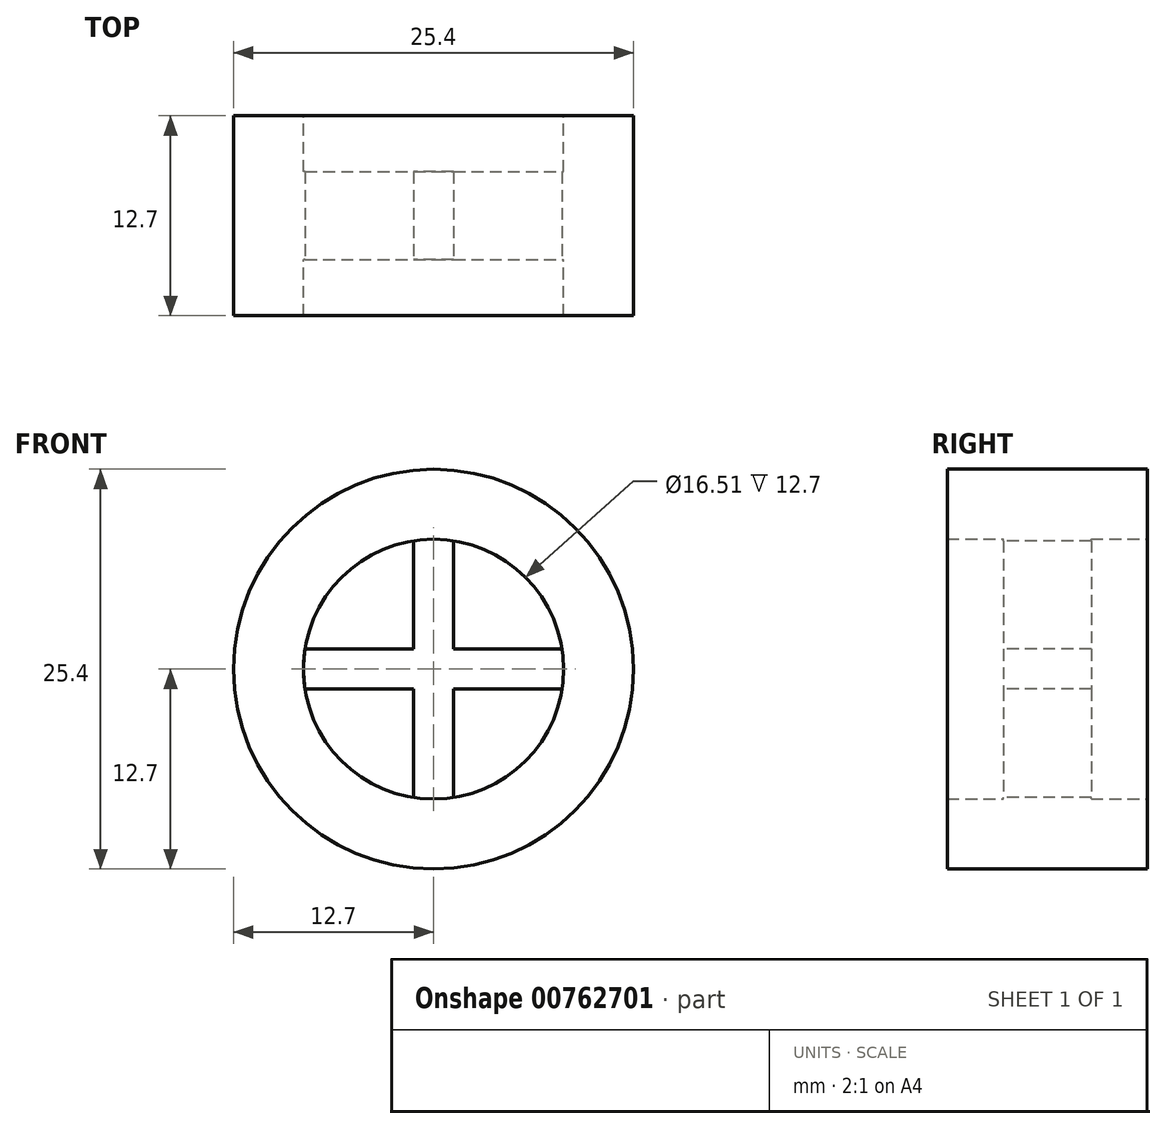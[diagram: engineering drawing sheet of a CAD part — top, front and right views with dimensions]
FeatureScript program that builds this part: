
annotation { "Feature Type Name" : "Feature", "Feature Type Description" : "" }
export const myFeature = defineFeature(function(context is Context, id is Id, definition is map)
    precondition{}
    {
        {
            var Q0;
            Q0=qCreatedBy(makeId("Front.planeOp"),FACE);
            var sketch = newSketch(context, id + "F0", { "sketchPlane" : qUnion([Q0])});
            skLineSegment(sketch, "E0", {"start": v(-26.37, 14.82) * mm, "end": v(-26.37, 24.82) * mm});
            skLineSegment(sketch, "E1", {"start": v(-26.37, 24.82) * mm, "end": v(-13.23, 24.82) * mm});
            skLineSegment(sketch, "E2", {"start": v(-13.23, 24.82) * mm, "end": v(-13.23, 15) * mm});
            skLineSegment(sketch, "E3", {"start": v(-13.23, 15) * mm, "end": v(-26.37, 14.82) * mm});
            skCircle(sketch, "E4", {"center": v(13.48, 17.4) * mm, "radius": 5.12 * mm});
            skPoint(sketch, "E4.first.point", {"position": v(10.66, 21.67) * mm});
            skPoint(sketch, "E4.second.point", {"position": v(16.03, 12.97) * mm});
            skPoint(sketch, "E4.third.point", {"position": v(17.5, 20.56) * mm});
            skLineSegment(sketch, "E5", {"start": v(10.66, 21.67) * mm, "end": v(13.48, 17.4) * mm});
            skLineSegment(sketch, "E6", {"start": v(17.5, 20.56) * mm, "end": v(13.48, 17.4) * mm});
            skLineSegment(sketch, "E7", {"start": v(13.48, 17.4) * mm, "end": v(16.03, 12.97) * mm});
            skLineSegment(sketch, "E8", {"start": v(9.35, 14.39) * mm, "end": v(13.48, 17.4) * mm});
            skCircle(sketch, "E9", {"center": v(0, 0) * mm, "radius": 12.7 * mm});
            skCircle(sketch, "E10", {"center": v(0, 0) * mm, "radius": 8.26 * mm});
            skLineSegment(sketch, "E11", {"start": v(-8.26, 0) * mm, "end": v(8.26, 0) * mm});
            skLineSegment(sketch, "E12", {"start": v(0, 8.26) * mm, "end": v(0, -8.26) * mm});
            skLineSegment(sketch, "E13", {"start": v(-1.27, 8.16) * mm, "end": v(-1.27, -8.26) * mm});
            skLineSegment(sketch, "E14", {"start": v(1.27, 8.16) * mm, "end": v(1.27, -8.16) * mm});
            skLineSegment(sketch, "E15", {"start": v(-8.16, 1.27) * mm, "end": v(8.16, 1.27) * mm});
            skLineSegment(sketch, "E16", {"start": v(-8.16, -1.27) * mm, "end": v(8.16, -1.27) * mm});
            skSolve(sketch);
        }
        {
            var Q0;
            Q0=makeQuery(id+"F0.imprint","IMPRINT",FACE,{"disambiguationData":[TD([[makeQuery(id+"F0.imprint","IMPRINT",EDGE,{"derivedFrom":sQuery(id+"F0.wireOp",EDGE,"E9")}),1.0]])]});
            extrude(context, id + "F1", {"entities" : qUnion([Q0]), "endBound" : BoundingType.SYMMETRIC, "depth" : 12.7 * mm, "offsetDistance" : 25.4 * mm});
        }
        {
            var Q0;
            {var subQ0=sQuery(id+"F0.wireOp",EDGE,"E12");var subQ1=sQuery(id+"F0.wireOp",EDGE,"E10");var subQ2=makeQuery(id+"F0.imprint","INTERSECT",VERTEX,{"disambiguationData":[OD(0.0)],"derivedFrom":[subQ1,subQ0]});Q0=makeQuery(id+"F0.imprint","IMPRINT",FACE,{"disambiguationData":[TD([[makeQuery(id+"F0.imprint","IMPRINT",EDGE,{"disambiguationData":[TD([[subQ2,1.0]])],"derivedFrom":subQ1}),1.0]])]});}
            var Q1;
            {var subQ0=sQuery(id+"F0.wireOp",EDGE,"E12");var subQ1=sQuery(id+"F0.wireOp",EDGE,"E10");var subQ2=makeQuery(id+"F0.imprint","INTERSECT",VERTEX,{"disambiguationData":[OD(0.0)],"derivedFrom":[subQ1,subQ0]});Q1=makeQuery(id+"F0.imprint","IMPRINT",FACE,{"disambiguationData":[TD([[makeQuery(id+"F0.imprint","IMPRINT",EDGE,{"disambiguationData":[TD([[subQ2,-1.0]])],"derivedFrom":subQ1}),1.0]])]});}
            var Q2;
            {var subQ0=sQuery(id+"F0.wireOp",EDGE,"E13");var subQ1=sQuery(id+"F0.wireOp",EDGE,"E11");var subQ2=makeQuery(id+"F0.imprint","INTERSECT",VERTEX,{"derivedFrom":[subQ1,subQ0]});Q2=makeQuery(id+"F0.imprint","IMPRINT",FACE,{"disambiguationData":[TD([[makeQuery(id+"F0.imprint","IMPRINT",EDGE,{"disambiguationData":[TD([[subQ2,-1.0]])],"derivedFrom":subQ1}),1.0]])]});}
            var Q3;
            {var subQ0=sQuery(id+"F0.wireOp",EDGE,"E12");var subQ1=sQuery(id+"F0.wireOp",EDGE,"E11");var subQ2=makeQuery(id+"F0.imprint","INTERSECT",VERTEX,{"derivedFrom":[subQ1,subQ0]});Q3=makeQuery(id+"F0.imprint","IMPRINT",FACE,{"disambiguationData":[TD([[makeQuery(id+"F0.imprint","IMPRINT",EDGE,{"disambiguationData":[TD([[subQ2,-1.0]])],"derivedFrom":subQ1}),1.0]])]});}
            var Q4;
            {var subQ0=sQuery(id+"F0.wireOp",EDGE,"E12");var subQ1=sQuery(id+"F0.wireOp",EDGE,"E11");var subQ2=makeQuery(id+"F0.imprint","INTERSECT",VERTEX,{"derivedFrom":[subQ1,subQ0]});Q4=makeQuery(id+"F0.imprint","IMPRINT",FACE,{"disambiguationData":[TD([[makeQuery(id+"F0.imprint","IMPRINT",EDGE,{"disambiguationData":[TD([[subQ2,-1.0]])],"derivedFrom":subQ1}),-1.0]])]});}
            var Q5;
            {var subQ0=sQuery(id+"F0.wireOp",EDGE,"E13");var subQ1=sQuery(id+"F0.wireOp",EDGE,"E11");var subQ2=makeQuery(id+"F0.imprint","INTERSECT",VERTEX,{"derivedFrom":[subQ1,subQ0]});Q5=makeQuery(id+"F0.imprint","IMPRINT",FACE,{"disambiguationData":[TD([[makeQuery(id+"F0.imprint","IMPRINT",EDGE,{"disambiguationData":[TD([[subQ2,-1.0]])],"derivedFrom":subQ1}),-1.0]])]});}
            var Q6;
            {var subQ0=sQuery(id+"F0.wireOp",EDGE,"E12");var subQ1=sQuery(id+"F0.wireOp",EDGE,"E10");var subQ2=makeQuery(id+"F0.imprint","INTERSECT",VERTEX,{"disambiguationData":[OD(1.0)],"derivedFrom":[subQ1,subQ0]});Q6=makeQuery(id+"F0.imprint","IMPRINT",FACE,{"disambiguationData":[TD([[makeQuery(id+"F0.imprint","IMPRINT",EDGE,{"disambiguationData":[TD([[subQ2,1.0]])],"derivedFrom":subQ1}),1.0]])]});}
            var Q7;
            {var subQ0=sQuery(id+"F0.wireOp",EDGE,"E12");var subQ1=sQuery(id+"F0.wireOp",EDGE,"E10");var subQ2=makeQuery(id+"F0.imprint","INTERSECT",VERTEX,{"disambiguationData":[OD(1.0)],"derivedFrom":[subQ1,subQ0]});Q7=makeQuery(id+"F0.imprint","IMPRINT",FACE,{"disambiguationData":[TD([[makeQuery(id+"F0.imprint","IMPRINT",EDGE,{"disambiguationData":[TD([[subQ2,-1.0]])],"derivedFrom":subQ1}),1.0]])]});}
            var Q8;
            {var subQ0=sQuery(id+"F0.wireOp",EDGE,"E11");var subQ1=sQuery(id+"F0.wireOp",EDGE,"E10");var subQ2=makeQuery(id+"F0.imprint","INTERSECT",VERTEX,{"disambiguationData":[OD(1.0)],"derivedFrom":[subQ1,subQ0]});Q8=makeQuery(id+"F0.imprint","IMPRINT",FACE,{"disambiguationData":[TD([[makeQuery(id+"F0.imprint","IMPRINT",EDGE,{"disambiguationData":[TD([[subQ2,1.0]])],"derivedFrom":subQ1}),1.0]])]});}
            var Q9;
            {var subQ0=sQuery(id+"F0.wireOp",EDGE,"E11");var subQ1=sQuery(id+"F0.wireOp",EDGE,"E10");var subQ2=makeQuery(id+"F0.imprint","INTERSECT",VERTEX,{"disambiguationData":[OD(1.0)],"derivedFrom":[subQ1,subQ0]});Q9=makeQuery(id+"F0.imprint","IMPRINT",FACE,{"disambiguationData":[TD([[makeQuery(id+"F0.imprint","IMPRINT",EDGE,{"disambiguationData":[TD([[subQ2,-1.0]])],"derivedFrom":subQ1}),1.0]])]});}
            var Q10;
            {var subQ0=sQuery(id+"F0.wireOp",EDGE,"E11");var subQ1=sQuery(id+"F0.wireOp",EDGE,"E10");var subQ2=makeQuery(id+"F0.imprint","INTERSECT",VERTEX,{"disambiguationData":[OD(0.0)],"derivedFrom":[subQ1,subQ0]});Q10=makeQuery(id+"F0.imprint","IMPRINT",FACE,{"disambiguationData":[TD([[makeQuery(id+"F0.imprint","IMPRINT",EDGE,{"disambiguationData":[TD([[subQ2,1.0]])],"derivedFrom":subQ1}),1.0]])]});}
            var Q11;
            {var subQ0=sQuery(id+"F0.wireOp",EDGE,"E11");var subQ1=sQuery(id+"F0.wireOp",EDGE,"E10");var subQ2=makeQuery(id+"F0.imprint","INTERSECT",VERTEX,{"disambiguationData":[OD(0.0)],"derivedFrom":[subQ1,subQ0]});Q11=makeQuery(id+"F0.imprint","IMPRINT",FACE,{"disambiguationData":[TD([[makeQuery(id+"F0.imprint","IMPRINT",EDGE,{"disambiguationData":[TD([[subQ2,-1.0]])],"derivedFrom":subQ1}),1.0]])]});}
            extrude(context, id + "F2", {"entities" : qUnion([Q0, Q1, Q2, Q3, Q4, Q5, Q6, Q7, Q8, Q9, Q10, Q11]), "operationType" : NewBodyOperationType.ADD, "endBound" : BoundingType.SYMMETRIC, "oppositeDirection" : true, "depth" : 5.6 * mm, "offsetDistance" : 25.4 * mm});
        }
    });
